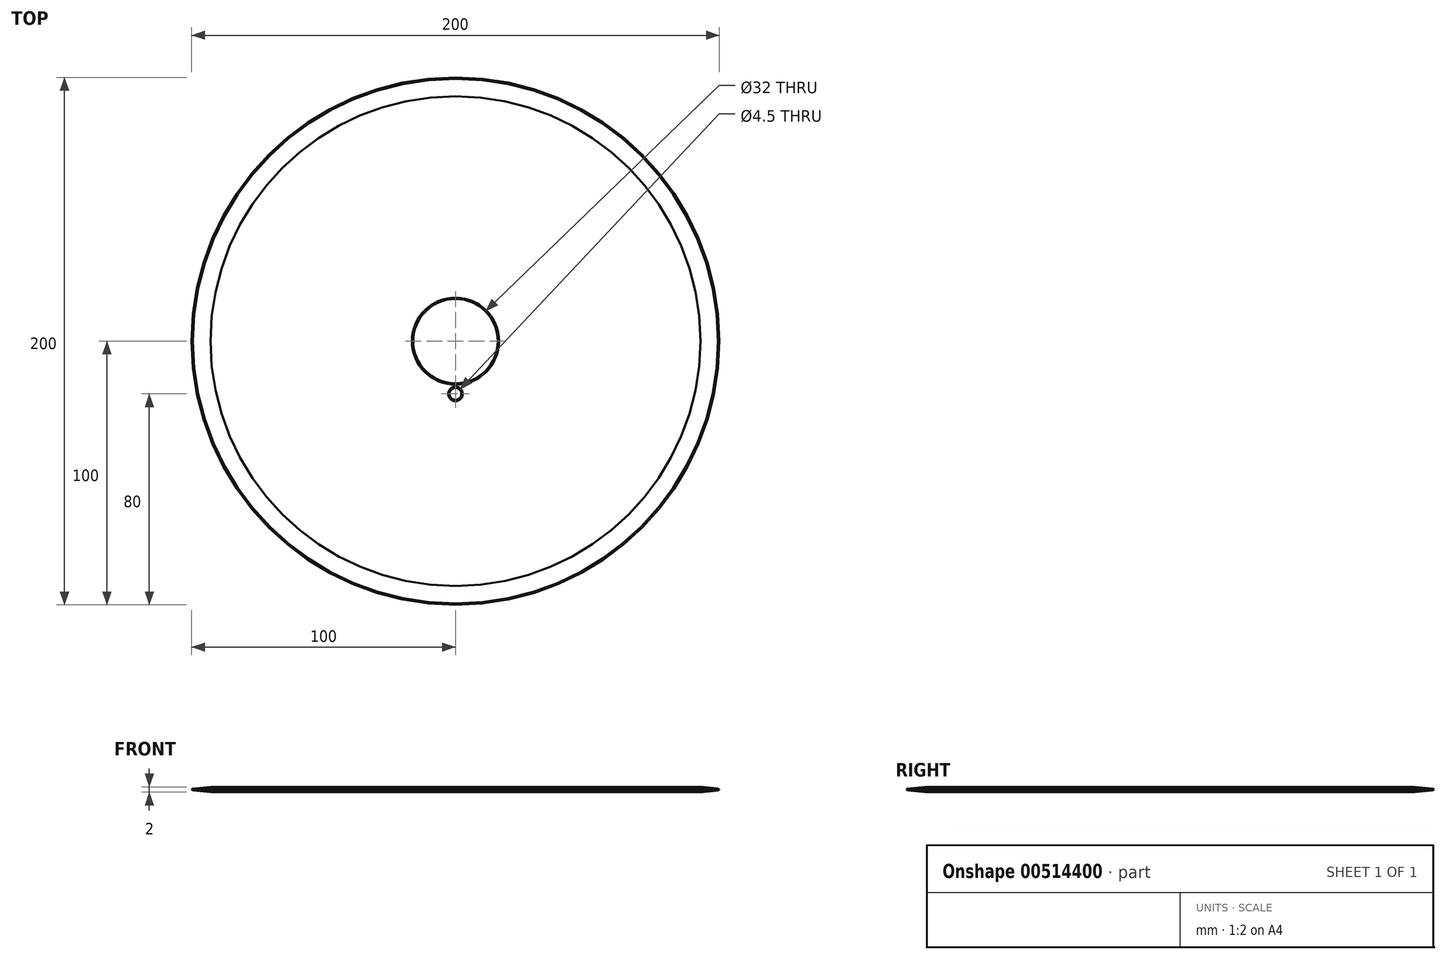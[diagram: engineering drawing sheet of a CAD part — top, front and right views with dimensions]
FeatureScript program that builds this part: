
annotation { "Feature Type Name" : "Feature", "Feature Type Description" : "" }
export const myFeature = defineFeature(function(context is Context, id is Id, definition is map)
    precondition{}
    {
        {
            var Q0;
            Q0=qCreatedBy(makeId("Top.planeOp"),FACE);
            var sketch = newSketch(context, id + "F0", { "sketchPlane" : qUnion([Q0])});
            skCircle(sketch, "E0", {"center": v(0, 0) * mm, "radius": 100 * mm});
            skCircle(sketch, "E1", {"center": v(0, 0) * mm, "radius": 16 * mm});
            skCircle(sketch, "E2", {"center": v(0, -20) * mm, "radius": 2.25 * mm});
            skSolve(sketch);
        }
        {
            var Q0;
            Q0=makeQuery(id+"F0.imprint","IMPRINT",FACE,{"disambiguationData":[TD([[makeQuery(id+"F0.imprint","IMPRINT",EDGE,{"derivedFrom":sQuery(id+"F0.wireOp",EDGE,"E0")}),1.0]])]});
            extrude(context, id + "F1", {"entities" : qUnion([Q0]), "endBound" : BoundingType.SYMMETRIC, "depth" : 2 * mm, "offsetDistance" : 25 * mm});
        }
        {
            var Q0;
            Q0=qCreatedBy(makeId("Right.planeOp"),FACE);
            var sketch = newSketch(context, id + "F2", { "sketchPlane" : qUnion([Q0])});
            skLineSegment(sketch, "E3", {"start": v(-100, -1.04) * mm, "end": v(-100, 1.04) * mm, "construction": true});
            skLineSegment(sketch, "E4", {"start": v(-100, 0) * mm, "end": v(-99.48, 0.3) * mm});
            skLineSegment(sketch, "E5", {"start": v(-99.48, 0.3) * mm, "end": v(-92.5, 1.04) * mm});
            skLineSegment(sketch, "E6", {"start": v(-100, 0) * mm, "end": v(-99.48, -0.3) * mm});
            skLineSegment(sketch, "E7", {"start": v(-99.48, -0.3) * mm, "end": v(-92.5, -1.04) * mm});
            skLineSegment(sketch, "E8", {"start": v(-100, 0) * mm, "end": v(-95.58, 0) * mm, "construction": true});
            skLineSegment(sketch, "E9", {"start": v(0, 0) * mm, "end": v(0, 9) * mm, "construction": true});
            skLineSegment(sketch, "E10", {"start": v(-100, 1.04) * mm, "end": v(-92.5, 1.04) * mm});
            skLineSegment(sketch, "E11", {"start": v(-100, 1.04) * mm, "end": v(-100, 0) * mm});
            skLineSegment(sketch, "E12", {"start": v(-100, 0) * mm, "end": v(-100, -1.04) * mm});
            skLineSegment(sketch, "E13", {"start": v(-92.5, -1.04) * mm, "end": v(-100, -1.04) * mm});
            skSolve(sketch);
        }
        {
            var Q0;
            Q0=makeQuery(id+"F2.imprint","IMPRINT",FACE,{"disambiguationData":[TD([[makeQuery(id+"F2.imprint","IMPRINT",EDGE,{"derivedFrom":sQuery(id+"F2.wireOp",EDGE,"E4")}),1.0]])]});
            var Q1;
            Q1=makeQuery(id+"F2.imprint","IMPRINT",FACE,{"disambiguationData":[TD([[makeQuery(id+"F2.imprint","IMPRINT",EDGE,{"derivedFrom":sQuery(id+"F2.wireOp",EDGE,"E6")}),-1.0]])]});
            var Q2;
            Q2=sQuery(id+"F2.wireOp",EDGE,"E9");
            revolve(context, id + "F3", {"operationType" : NewBodyOperationType.REMOVE, "entities" : qUnion([Q0, Q1]), "axis" : qUnion([Q2]), "revolveType" : RevolveType.FULL, "oppositeDirection" : true});
        }
        {
            var Q0;
            Q0=makeQuery(id+"F1.opExtrude","CAP_EDGE",EDGE,{"disambiguationData":[OSD([sQuery(id+"F0.wireOp",EDGE,"E1")])],"isStart":false});
            var Q1;
            Q1=makeQuery(id+"F1.opExtrude","CAP_EDGE",EDGE,{"disambiguationData":[OSD([sQuery(id+"F0.wireOp",EDGE,"E1")])],"isStart":true});
            var Q2;
            Q2=makeQuery(id+"F1.opExtrude","CAP_EDGE",EDGE,{"disambiguationData":[OSD([sQuery(id+"F0.wireOp",EDGE,"E2")])],"isStart":false});
            var Q3;
            Q3=makeQuery(id+"F1.opExtrude","CAP_EDGE",EDGE,{"disambiguationData":[OSD([sQuery(id+"F0.wireOp",EDGE,"E2")])],"isStart":true});
            chamfer(context, id + "F4", {"entities" : qUnion([Q0, Q1, Q2, Q3]), "width" : 0.5 * mm, "tangentPropagation" : true});
        }
    });
